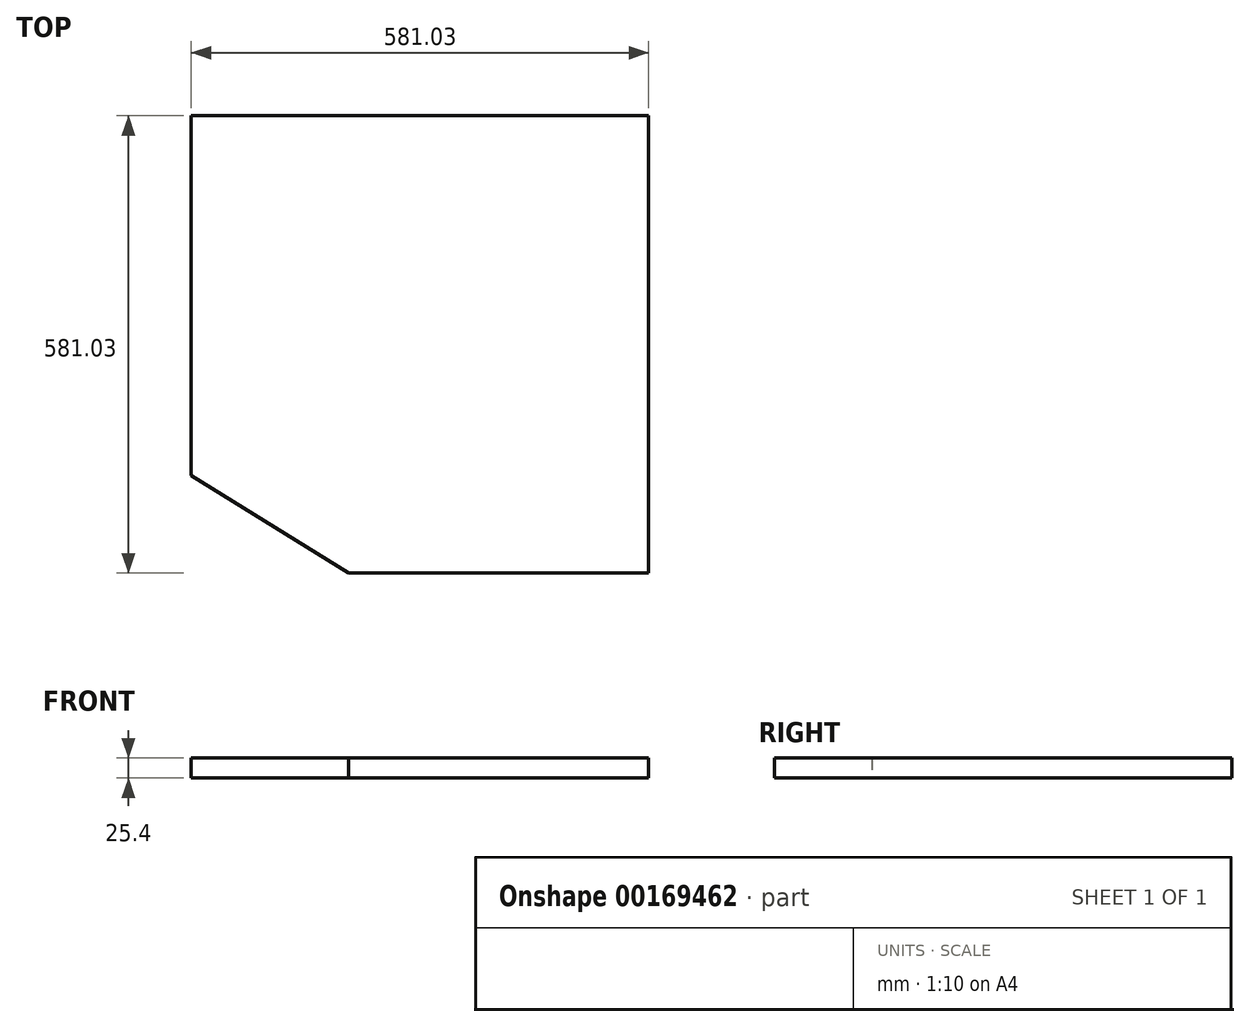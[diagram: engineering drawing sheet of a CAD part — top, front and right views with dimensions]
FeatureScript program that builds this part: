
annotation { "Feature Type Name" : "Feature", "Feature Type Description" : "" }
export const myFeature = defineFeature(function(context is Context, id is Id, definition is map)
    precondition{}
    {
        {
            var Q0;
            Q0=qCreatedBy(makeId("Top.planeOp"),FACE);
            var sketch = newSketch(context, id + "F0", { "sketchPlane" : qUnion([Q0])});
            skLineSegment(sketch, "E0", {"start": v(-428.75, 0) * mm, "end": v(152.28, 0) * mm});
            skLineSegment(sketch, "E1", {"start": v(152.28, 0) * mm, "end": v(152.28, -581.02) * mm});
            skLineSegment(sketch, "E2", {"start": v(152.28, -581.02) * mm, "end": v(-228.72, -581.02) * mm});
            skLineSegment(sketch, "E3", {"start": v(-228.72, -581.02) * mm, "end": v(-428.75, -457.2) * mm});
            skLineSegment(sketch, "E4", {"start": v(-428.75, -457.2) * mm, "end": v(-428.75, 0) * mm});
            skSolve(sketch);
        }
        {
            var Q0;
            Q0 = qSketchRegion(id + "F0", true);
            extrude(context, id + "F1", {"entities" : qUnion([Q0]), "depth" : 25.4 * mm});
        }
    });
